MODEL slx_73f4d7f3f829
CONFIG AbsTol = auto
CONFIG FixedStep = 0.01
CONFIG MaxStep = auto
CONFIG MinStep = auto
CONFIG RelTol = 1e-3
CONFIG SampleTimeConstraint = Unconstrained
CONFIG Solver = FixedStepDiscrete
CONFIG SolverMode = Auto
CONFIG SolverName = FixedStepDiscrete
CONFIG StartTime = 0.0
CONFIG StopTime = 10.0
BLOCK [Scope] Scope
  NumInputPorts = 3
  Ports = [3]
  ScopeSpecificationString = Simulink.scopes.TimeScopeBlockCfg('CurrentConfiguration', extmgr.ConfigurationSet(extmgr.Configuration('Core','General UI',true),extmgr.Configuration('Core','Source UI',true),extmgr.Configuration('Sources','WiredSimulink',true,'DataLoggingSaveFormat','StructureWithTime','DataLoggingLimitDataPoints',true,'DataLoggingDecimation','1','DataLoggingDecimateData',true),extmgr.Configuration('Visuals','Tim...<+2996ch>
BLOCK [Scope] Scope1
  IOType = viewer
  Ports = []
  ScopeSpecificationString = Simulink.scopes.TimeScopeBlockCfg('CurrentConfiguration', extmgr.ConfigurationSet(extmgr.Configuration('Core','General UI',true),extmgr.Configuration('Core','Source UI',true),extmgr.Configuration('Sources','WiredSimulink',true,'DataLoggingMaxPoints','7500','DataLoggingLimitDataPoints',true,'DataLoggingSaveFormat','Array','DataLoggingDecimation','1','DataLoggingDecimateData',true),extmgr.Configurat...<+2938ch>
BLOCK [Scope] Scope2
  IOType = viewer
  Ports = []
  ScopeSpecificationString = C++SS(StrPVP('Location','[430, 426, 857, 665]'),StrPVP('Open','off'),MxPVP('AxesTitles',24,'struct(''axes1'',''%<SignalLabel>'',''axes2'',''%<SignalLabel>'',''axes3'',''%<SignalLabel>'')'),StrPVP('ShowDataMarkers','off'),StrPVP('ShowLegends','off'),StrPVP('YMin','-5~-5~-5'),StrPVP('YMax','5~5~5'),StrPVP('SaveName','ScopeData1'),StrPVP('MaxDataPoints','7500'),StrPVP('LimitDataPoints','on'),StrPVP('...<+84ch>
BLOCK [Scope] Scope3
  IOType = viewer
  Ports = []
  ScopeSpecificationString = C++SS(StrPVP('Location','[188, 365, 512, 604]'),StrPVP('Open','off'),MxPVP('AxesTitles',24,'struct(''axes1'',''%<SignalLabel>'')'),StrPVP('ShowDataMarkers','off'),StrPVP('ShowLegends','off'),StrPVP('SaveName','ScopeData2'),StrPVP('MaxDataPoints','7500'),StrPVP('LimitDataPoints','on'),StrPVP('DataFormat','Array'),StrPVP('Decimation','1'),StrPVP('BlockParamSampleInput','off'))
BLOCK [SubSystem] Signal Builder
  ClipboardFcn = sigbuilder_block('clipboard');
  CloseFcn = sigbuilder_block('close');
  ContinueFcn = sigbuilder_block('continue');
  CopyFcn = sigbuilder_block('copy');
  DeleteFcn = sigbuilder_block('delete');
  LoadFcn = sigbuilder_block('load');
  MaskHideContents = on
  ModelCloseFcn = sigbuilder_block('modelClose');
  NameChangeFcn = sigbuilder_block('namechange');
  OpenFcn = sigbuilder_block('open',[237.75 92.25 550.5 357 ]);
  PauseFcn = sigbuilder_block('pause');
  Ports = [0, 3]
  PreSaveFcn = sigbuilder_block('preSave');
  RequestExecContextInheritance = off
  StartFcn = sigbuilder_block('start');
  StopFcn = sigbuilder_block('stop');
  Tag = STV Subsys
  Variant = off
BLOCK [Demux] Signal Builder/Demux
  Outputs = 3
  Ports = [1, 3]
  Tag = STV Demux
BLOCK [FromWorkspace] Signal Builder/FromWs
  SampleTime = 0
  Tag = STV FromWs
  VariableName = tuvar
  ZeroCross = on
BLOCK [Outport] Signal Builder/Signal 1
  IconDisplay = Port number
  Tag = STV Outport
BLOCK [Outport] Signal Builder/Signal 2
  IconDisplay = Port number
  Port = 2
  Tag = STV Outport
BLOCK [Outport] Signal Builder/Signal 3
  IconDisplay = Port number
  Port = 3
  Tag = STV Outport
LINE Signal Builder:1 -> Scope:1
LINE Signal Builder:2 -> Scope:2
LINE Signal Builder:3 -> Scope:3
